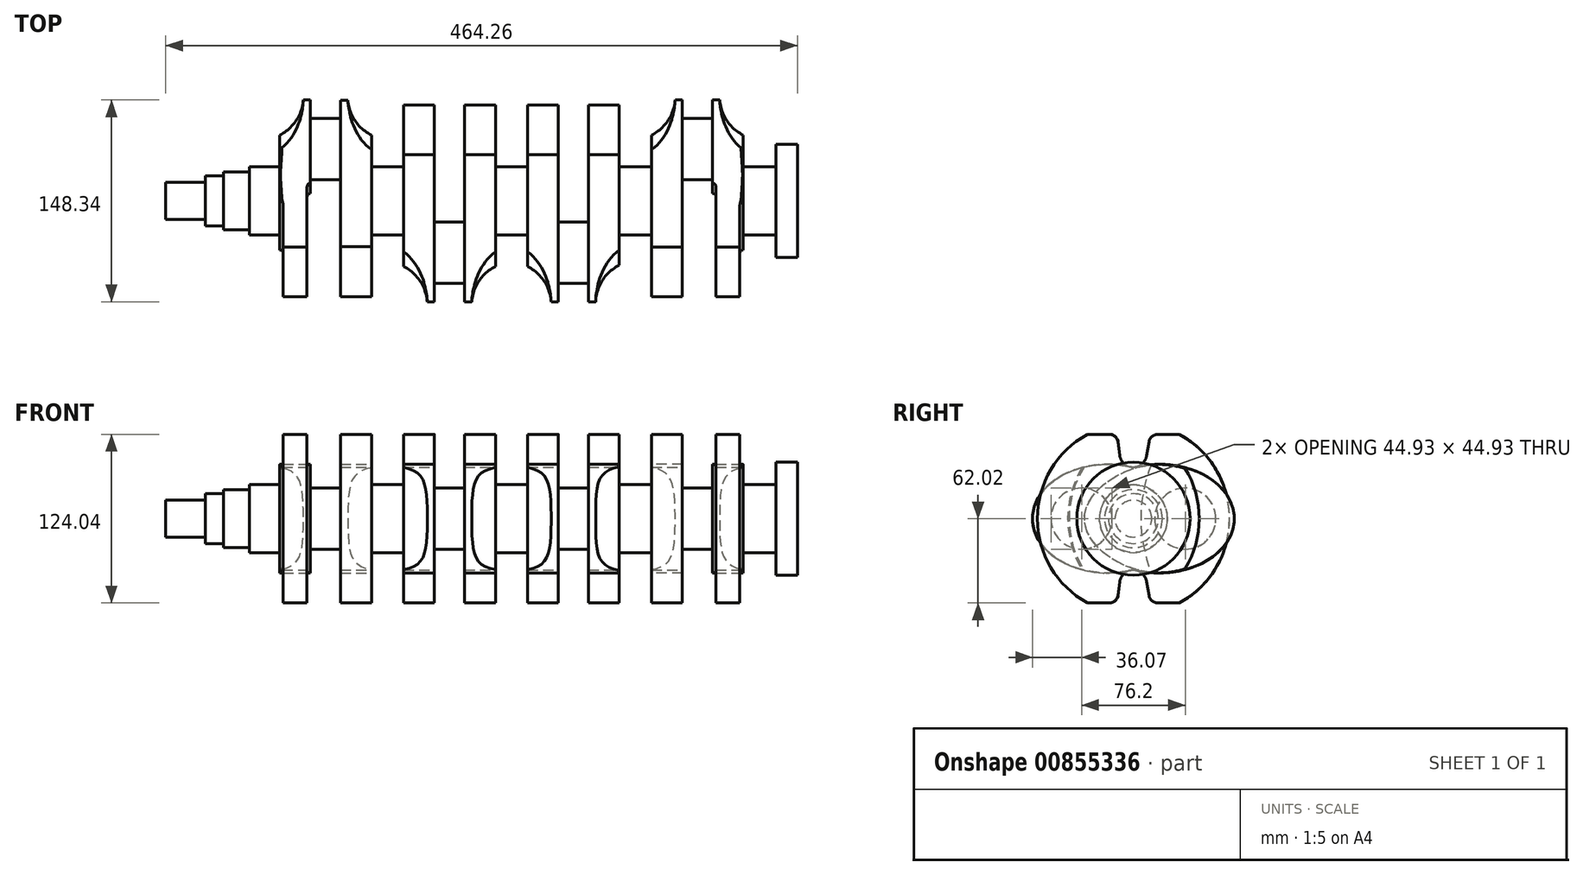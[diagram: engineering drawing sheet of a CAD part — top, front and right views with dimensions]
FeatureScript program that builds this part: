
annotation { "Feature Type Name" : "Feature", "Feature Type Description" : "" }
export const myFeature = defineFeature(function(context is Context, id is Id, definition is map)
    precondition{}
    {
        {
            var Q0;
            Q0=qCreatedBy(makeId("Right.planeOp"),FACE);
            var sketch = newSketch(context, id + "F0", { "sketchPlane" : qUnion([Q0])});
            skLineSegment(sketch, "E0", {"start": v(0, 0) * mm, "end": v(38.1, 0) * mm});
            skLineSegment(sketch, "E1.MirrorCS", {"start": v(0, 0) * mm, "end": v(-38.1, 0) * mm});
            skSolve(sketch);
        }
        {
            var Q0;
            Q0=qCreatedBy(makeId("Front.planeOp"),FACE);
            var sketch = newSketch(context, id + "F1", { "sketchPlane" : qUnion([Q0])});
            skLineSegment(sketch, "E2", {"start": v(-192.37, 24.97) * mm, "end": v(-176.5, 24.97) * mm});
            skLineSegment(sketch, "E3", {"start": v(194.75, 24.97) * mm, "end": v(194.75, 41.6) * mm});
            skLineSegment(sketch, "E4", {"start": v(194.75, 41.6) * mm, "end": v(210.48, 41.6) * mm});
            skLineSegment(sketch, "E5", {"start": v(210.48, 41.6) * mm, "end": v(210.48, 0) * mm});
            skLineSegment(sketch, "E6", {"start": v(-192.37, 24.97) * mm, "end": v(-192.37, 21.27) * mm});
            skLineSegment(sketch, "E7", {"start": v(-192.37, 21.27) * mm, "end": v(-211.42, 21.27) * mm});
            skLineSegment(sketch, "E8", {"start": v(-211.42, 21.27) * mm, "end": v(-211.42, 18.3) * mm});
            skLineSegment(sketch, "E9", {"start": v(-211.42, 18.3) * mm, "end": v(-224.88, 18.3) * mm});
            skLineSegment(sketch, "E10", {"start": v(-224.88, 18.3) * mm, "end": v(-224.88, 13.53) * mm});
            skLineSegment(sketch, "E11", {"start": v(-224.88, 13.53) * mm, "end": v(-253.78, 13.53) * mm});
            skLineSegment(sketch, "E12", {"start": v(-253.78, 0) * mm, "end": v(-253.78, 13.53) * mm});
            skLineSegment(sketch, "E13", {"start": v(-253.78, 0) * mm, "end": v(-176.5, 0) * mm});
            skLineSegment(sketch, "E14.MirrorCS", {"start": v(-192.37, -24.97) * mm, "end": v(194.75, -24.97) * mm, "construction": true});
            skLineSegment(sketch, "E15.MirrorCS", {"start": v(-192.37, -21.27) * mm, "end": v(-211.42, -21.27) * mm, "construction": true});
            skLineSegment(sketch, "E16.MirrorCS", {"start": v(-211.42, -18.3) * mm, "end": v(-224.88, -18.3) * mm, "construction": true});
            skLineSegment(sketch, "E17.MirrorCS", {"start": v(-224.88, -13.53) * mm, "end": v(-253.78, -13.53) * mm, "construction": true});
            skLineSegment(sketch, "E18.MirrorCS", {"start": v(194.75, -41.6) * mm, "end": v(210.48, -41.6) * mm, "construction": true});
            skLineSegment(sketch, "E19", {"start": v(194.75, 24.97) * mm, "end": v(194.75, 0) * mm});
            skLineSegment(sketch, "E20.trimOffspring", {"start": v(194.75, 0) * mm, "end": v(210.48, 0) * mm});
            skLineSegment(sketch, "E21.bottom", {"start": v(-192.37, 24.97) * mm, "end": v(-170.08, 24.97) * mm});
            skLineSegment(sketch, "E21.top", {"start": v(-192.37, 0) * mm, "end": v(-170.08, 0) * mm});
            skLineSegment(sketch, "E21.right", {"start": v(-170.08, 24.97) * mm, "end": v(-170.08, 0) * mm});
            skLineSegment(sketch, "E22", {"start": v(-170.08, 0) * mm, "end": v(194.75, 0) * mm, "construction": true});
            skLineSegment(sketch, "E23", {"start": v(-170.08, 24.97) * mm, "end": v(194.75, 24.97) * mm, "construction": true});
            skLineSegment(sketch, "E24", {"start": v(-170.08, 0) * mm, "end": v(-170.08, -145.17) * mm, "construction": true});
            skLineSegment(sketch, "E25", {"start": v(-170.08, -145.17) * mm, "end": v(-135.68, -145.17) * mm, "construction": true});
            skLineSegment(sketch, "E26", {"start": v(-135.68, -145.17) * mm, "end": v(-135.68, 174.11) * mm, "construction": true});
            skLineSegment(sketch, "E27", {"start": v(-135.68, 174.11) * mm, "end": v(-170.08, 174.11) * mm, "construction": true});
            skLineSegment(sketch, "E28", {"start": v(-170.08, 174.11) * mm, "end": v(-170.08, 24.97) * mm, "construction": true});
            skSolve(sketch);
        }
        {
            var Q0;
            Q0 = qSketchRegion(id + "F1", true);
            var Q1;
            Q1=sQuery(id+"F1.wireOp",EDGE,"E13");
            revolve(context, id + "F2", {"surfaceOperationType" : NewSurfaceOperationType.NEW, "entities" : qUnion([Q0]), "axis" : qUnion([Q1]), "revolveType" : RevolveType.FULL});
        }
        {
            var Q0;
            Q0=makeQuery(id+"F2.opRevolve","SWEPT_FACE",FACE,{"disambiguationData":[OSD([sQuery(id+"F1.wireOp",EDGE,"E6")])]});
            cPlane(context, id + "F3", {"entities" : qUnion([Q0]), "cplaneType" : CPlaneType.OFFSET, "offset" : 33.62 * mm, "oppositeDirection" : true, "width" : 150 * mm, "height" : 150 * mm});
        }
        {
            var Q0;
            Q0=qCreatedBy(id+"F3.planeOp",FACE);
            var sketch = newSketch(context, id + "F4", { "sketchPlane" : qUnion([Q0])});
            skLineSegment(sketch, "E29", {"start": v(-74.17, 0) * mm, "end": v(74.61, 0) * mm, "construction": true});
            skArc(sketch, "E30", {"start": v(33.95, -61.91) * mm, "mid": v(70.61, 0) * mm, "end": v(33.95, 61.91) * mm});
            skLineSegment(sketch, "E31", {"start": v(33.95, 61.91) * mm, "end": v(17.7, 61.91) * mm});
            skLineSegment(sketch, "E32", {"start": v(33.95, -61.91) * mm, "end": v(17.7, -61.91) * mm});
            skArc(sketch, "E33", {"start": v(17.7, 61.91) * mm, "mid": v(13.5, 60.33) * mm, "end": v(11.4, 56.38) * mm});
            skPoint(sketch, "E34.orphan", {"position": v(-76.24, 0) * mm});
            skEllipticalArc(sketch, "E35", {});
            skPoint(sketch, "E36.orphan", {"position": v(-19.05, 39.95) * mm});
            skPoint(sketch, "E37.end.orphan", {"position": v(-17.72, -39.94) * mm});
            skLineSegment(sketch, "E38", {"start": v(10.13, 46.63) * mm, "end": v(11.4, 56.38) * mm});
            skArc(sketch, "E39", {"start": v(-2.24, 38.04) * mm, "mid": v(5.85, 39.6) * mm, "end": v(10.13, 46.63) * mm});
            skArc(sketch, "E40.MirrorCS", {"start": v(17.7, -61.91) * mm, "mid": v(13.5, -60.33) * mm, "end": v(11.4, -56.38) * mm});
            skLineSegment(sketch, "E41.MirrorCS", {"start": v(10.13, -46.63) * mm, "end": v(11.4, -56.38) * mm});
            skArc(sketch, "E42.MirrorCS", {"start": v(-2.24, -38.04) * mm, "mid": v(5.85, -39.6) * mm, "end": v(10.13, -46.63) * mm});
            const initialGuessF4  = {"E35": [-0.01905, 0, -1, 0, 0.055118, 0.03994730190328979, 4.402440832772506, 1.88074447440708]};
            skSetInitialGuess(sketch, initialGuessF4);
            skSolve(sketch);
        }
        {
            var Q0;
            Q0=qCreatedBy(id+"F3.planeOp",FACE);
            cPlane(context, id + "F5", {"entities" : qUnion([Q0]), "cplaneType" : CPlaneType.OFFSET, "offset" : 44.8 * mm, "oppositeDirection" : true, "width" : 150 * mm, "height" : 150 * mm});
        }
        {
            var Q0;
            Q0=qCreatedBy(id+"F5.planeOp",FACE);
            var sketch = newSketch(context, id + "F6", { "sketchPlane" : qUnion([Q0])});
            skEllipticalArc(sketch, "E43", {});
            skArc(sketch, "E44", {"start": v(33.75, -62.02) * mm, "mid": v(70.61, 0) * mm, "end": v(33.75, 62.02) * mm});
            skArc(sketch, "E45", {"start": v(-2.04, 38.05) * mm, "mid": v(6.22, 39.73) * mm, "end": v(10.37, 47.06) * mm});
            skLineSegment(sketch, "E46", {"start": v(17.5, 62.02) * mm, "end": v(33.75, 62.02) * mm});
            skArc(sketch, "E47", {"start": v(17.5, 62.02) * mm, "mid": v(13.2, 60.35) * mm, "end": v(11.17, 56.22) * mm});
            skLineSegment(sketch, "E48", {"start": v(10.37, 47.06) * mm, "end": v(11.17, 56.22) * mm});
            skLineSegment(sketch, "E49.MirrorCS", {"start": v(17.5, -62.02) * mm, "end": v(33.75, -62.02) * mm});
            skArc(sketch, "E50.MirrorCS", {"start": v(17.5, -62.02) * mm, "mid": v(13.2, -60.35) * mm, "end": v(11.17, -56.22) * mm});
            skLineSegment(sketch, "E51.MirrorCS", {"start": v(10.37, -47.06) * mm, "end": v(11.17, -56.22) * mm});
            skArc(sketch, "E52.MirrorCS", {"start": v(-2.04, -38.05) * mm, "mid": v(6.22, -39.73) * mm, "end": v(10.37, -47.06) * mm});
            const initialGuessF6  = {"E43": [-0.018827772470886794, 0, -1, 0, 0.055118, 0.03994730190328979, 4.402958475438665, 1.8807444744070803]};
            skSetInitialGuess(sketch, initialGuessF6);
            skSolve(sketch);
        }
        {
            var Q0;
            Q0=qCreatedBy(id+"F5.planeOp",FACE);
            cPlane(context, id + "F7", {"entities" : qUnion([Q0]), "cplaneType" : CPlaneType.OFFSET, "offset" : 46.31 * mm, "oppositeDirection" : true, "width" : 150 * mm, "height" : 150 * mm});
        }
        {
            var Q0;
            Q0=qCreatedBy(id+"F7.planeOp",FACE);
            var sketch = newSketch(context, id + "F8", { "sketchPlane" : qUnion([Q0])});
            skLineSegment(sketch, "E53", {"start": v(-128.9, 0) * mm, "end": v(74.17, 0) * mm, "construction": true});
            skArc(sketch, "E54", {"start": v(-33.95, 61.91) * mm, "mid": v(-70.61, 0) * mm, "end": v(-33.95, -61.91) * mm});
            skLineSegment(sketch, "E55", {"start": v(74.17, 61.8) * mm, "end": v(74.17, -79.85) * mm, "construction": true});
            skLineSegment(sketch, "E56.trimOffspring", {"start": v(19.08, 39.94) * mm, "end": v(19.08, -39.94) * mm, "construction": true});
            skEllipticalArc(sketch, "E57", {});
            skLineSegment(sketch, "E58", {"start": v(-33.95, 61.91) * mm, "end": v(-17.7, 61.91) * mm});
            skArc(sketch, "E59", {"start": v(-11.4, 56.42) * mm, "mid": v(-13.52, 60.35) * mm, "end": v(-17.7, 61.91) * mm});
            skArc(sketch, "E60", {"start": v(-10.07, 46.57) * mm, "mid": v(-5.77, 39.58) * mm, "end": v(2.3, 38.04) * mm});
            skLineSegment(sketch, "E61", {"start": v(-10.07, 46.57) * mm, "end": v(-11.4, 56.42) * mm});
            skLineSegment(sketch, "E62.MirrorCS", {"start": v(-33.95, -61.91) * mm, "end": v(-17.7, -61.91) * mm});
            skLineSegment(sketch, "E63.MirrorCS", {"start": v(-10.07, -46.57) * mm, "end": v(-11.4, -56.42) * mm});
            skArc(sketch, "E64.MirrorCS", {"start": v(-10.07, -46.57) * mm, "mid": v(-5.77, -39.58) * mm, "end": v(2.3, -38.04) * mm});
            skArc(sketch, "E65.MirrorCS", {"start": v(-11.4, -56.42) * mm, "mid": v(-13.52, -60.35) * mm, "end": v(-17.7, -61.91) * mm});
            const initialGuessF8  = {"E57": [0.019076767620736908, 0, 1, 0, 0.05509123237926309, 0.03994149999999999, 4.4028504044055, 1.8803349027740879]};
            skSetInitialGuess(sketch, initialGuessF8);
            skSolve(sketch);
        }
        {
            var Q0;
            Q0=qCreatedBy(id+"F7.planeOp",FACE);
            cPlane(context, id + "F9", {"entities" : qUnion([Q0]), "cplaneType" : CPlaneType.OFFSET, "offset" : 44.8 * mm, "oppositeDirection" : true, "width" : 150 * mm, "height" : 150 * mm});
        }
        {
            var Q0;
            Q0=qCreatedBy(id+"F9.planeOp",FACE);
            var sketch = newSketch(context, id + "F10", { "sketchPlane" : qUnion([Q0])});
            skArc(sketch, "E66", {"start": v(-33.95, 61.91) * mm, "mid": v(-70.61, 0) * mm, "end": v(-33.95, -61.91) * mm});
            skLineSegment(sketch, "E67", {"start": v(-140.28, 0) * mm, "end": v(97.25, 0) * mm, "construction": true});
            skLineSegment(sketch, "E68", {"start": v(19.05, 39.94) * mm, "end": v(19.05, 0) * mm, "construction": true});
            skPoint(sketch, "E69.trimOffspring.end.orphan", {"position": v(55.02, 61.91) * mm});
            skPoint(sketch, "E70.start.orphan", {"position": v(-109.8, 61.91) * mm});
            skPoint(sketch, "E71.orphan", {"position": v(-109.8, -61.91) * mm});
            skPoint(sketch, "E72.MirrorCS.end.orphan", {"position": v(55.02, -61.91) * mm});
            skEllipticalArc(sketch, "E73", {});
            skLineSegment(sketch, "E74", {"start": v(-33.95, 61.91) * mm, "end": v(-17.7, 61.91) * mm});
            skArc(sketch, "E75", {"start": v(-17.7, 61.91) * mm, "mid": v(-13.6, 60.4) * mm, "end": v(-11.43, 56.6) * mm});
            skLineSegment(sketch, "E76", {"start": v(-11.43, 56.6) * mm, "end": v(-9.73, 46.35) * mm});
            skArc(sketch, "E77", {"start": v(-9.73, 46.35) * mm, "mid": v(-5.37, 39.58) * mm, "end": v(2.55, 38.1) * mm});
            skArc(sketch, "E78.MirrorCS", {"start": v(-9.73, -46.35) * mm, "mid": v(-5.37, -39.58) * mm, "end": v(2.55, -38.1) * mm});
            skLineSegment(sketch, "E79.MirrorCS", {"start": v(-11.43, -56.6) * mm, "end": v(-9.73, -46.35) * mm});
            skArc(sketch, "E80.MirrorCS", {"start": v(-17.7, -61.91) * mm, "mid": v(-13.6, -60.4) * mm, "end": v(-11.43, -56.6) * mm});
            skLineSegment(sketch, "E81.MirrorCS", {"start": v(-33.95, -61.91) * mm, "end": v(-17.7, -61.91) * mm});
            const initialGuessF10  = {"E73": [0.01905, 0, 1, 0, 0.055118, 0.039941500000000005, 4.408302439790269, 1.8748828673893172]};
            skSetInitialGuess(sketch, initialGuessF10);
            skSolve(sketch);
        }
        {
            var Q0;
            Q0=qCreatedBy(id+"F9.planeOp",FACE);
            cPlane(context, id + "F11", {"entities" : qUnion([Q0]), "cplaneType" : CPlaneType.OFFSET, "offset" : 46.31 * mm, "oppositeDirection" : true, "width" : 150 * mm, "height" : 150 * mm});
        }
        {
            var Q0;
            Q0=qCreatedBy(id+"F11.planeOp",FACE);
            var sketch = newSketch(context, id + "F12", { "sketchPlane" : qUnion([Q0])});
            skArc(sketch, "E82", {"start": v(-33.95, 61.91) * mm, "mid": v(-70.61, 0) * mm, "end": v(-33.95, -61.91) * mm});
            skLineSegment(sketch, "E83", {"start": v(-140.28, 0) * mm, "end": v(97.25, 0) * mm, "construction": true});
            skLineSegment(sketch, "E84", {"start": v(19.05, 39.94) * mm, "end": v(19.05, 0) * mm, "construction": true});
            skPoint(sketch, "E85.trimOffspring.end.orphan", {"position": v(69.73, 63.16) * mm});
            skPoint(sketch, "E86.start.orphan", {"position": v(-95.09, 63.16) * mm});
            skPoint(sketch, "E87.orphan", {"position": v(-95.09, -63.16) * mm});
            skPoint(sketch, "E88.MirrorCS.end.orphan", {"position": v(69.73, -63.16) * mm});
            skEllipticalArc(sketch, "E89", {});
            skLineSegment(sketch, "E90", {"start": v(-33.95, 61.91) * mm, "end": v(-17.7, 61.91) * mm});
            skArc(sketch, "E91", {"start": v(-17.7, 61.91) * mm, "mid": v(-13.6, 60.4) * mm, "end": v(-11.43, 56.6) * mm});
            skLineSegment(sketch, "E92", {"start": v(-11.43, 56.6) * mm, "end": v(-9.73, 46.35) * mm});
            skArc(sketch, "E93", {"start": v(-9.73, 46.35) * mm, "mid": v(-5.37, 39.58) * mm, "end": v(2.55, 38.1) * mm});
            skArc(sketch, "E94.MirrorCS", {"start": v(-9.73, -46.35) * mm, "mid": v(-5.37, -39.58) * mm, "end": v(2.55, -38.1) * mm});
            skLineSegment(sketch, "E95.MirrorCS", {"start": v(-11.43, -56.6) * mm, "end": v(-9.73, -46.35) * mm});
            skArc(sketch, "E96.MirrorCS", {"start": v(-17.7, -61.91) * mm, "mid": v(-13.6, -60.4) * mm, "end": v(-11.43, -56.6) * mm});
            skLineSegment(sketch, "E97.MirrorCS", {"start": v(-33.95, -61.91) * mm, "end": v(-17.7, -61.91) * mm});
            const initialGuessF12  = {"E89": [0.01905, 0, 1, 0, 0.055118, 0.039941500000000005, 4.408302439790269, 1.8748828673893168]};
            skSetInitialGuess(sketch, initialGuessF12);
            skSolve(sketch);
        }
        {
            var Q0;
            Q0=qCreatedBy(id+"F11.planeOp",FACE);
            cPlane(context, id + "F13", {"entities" : qUnion([Q0]), "cplaneType" : CPlaneType.OFFSET, "offset" : 44.8 * mm, "oppositeDirection" : true, "width" : 150 * mm, "height" : 150 * mm});
        }
        {
            var Q0;
            Q0=qCreatedBy(id+"F13.planeOp",FACE);
            var sketch = newSketch(context, id + "F14", { "sketchPlane" : qUnion([Q0])});
            skArc(sketch, "E98", {"start": v(-33.95, 61.91) * mm, "mid": v(-70.61, 0) * mm, "end": v(-33.95, -61.91) * mm});
            skLineSegment(sketch, "E99", {"start": v(-140.28, 0) * mm, "end": v(97.25, 0) * mm, "construction": true});
            skLineSegment(sketch, "E100", {"start": v(19.05, 39.94) * mm, "end": v(19.05, 0) * mm, "construction": true});
            skPoint(sketch, "E101.trimOffspring.end.orphan", {"position": v(69.73, 63.16) * mm});
            skPoint(sketch, "E102.start.orphan", {"position": v(-95.09, 63.16) * mm});
            skPoint(sketch, "E103.orphan", {"position": v(-95.09, -63.16) * mm});
            skPoint(sketch, "E104.MirrorCS.end.orphan", {"position": v(69.73, -63.16) * mm});
            skEllipticalArc(sketch, "E105", {});
            skLineSegment(sketch, "E106", {"start": v(-33.95, 61.91) * mm, "end": v(-17.7, 61.91) * mm});
            skArc(sketch, "E107", {"start": v(-17.7, 61.91) * mm, "mid": v(-13.6, 60.4) * mm, "end": v(-11.43, 56.6) * mm});
            skLineSegment(sketch, "E108", {"start": v(-11.43, 56.6) * mm, "end": v(-9.73, 46.35) * mm});
            skArc(sketch, "E109", {"start": v(-9.73, 46.35) * mm, "mid": v(-5.37, 39.58) * mm, "end": v(2.55, 38.1) * mm});
            skArc(sketch, "E110.MirrorCS", {"start": v(-9.73, -46.35) * mm, "mid": v(-5.37, -39.58) * mm, "end": v(2.55, -38.1) * mm});
            skLineSegment(sketch, "E111.MirrorCS", {"start": v(-11.43, -56.6) * mm, "end": v(-9.73, -46.35) * mm});
            skArc(sketch, "E112.MirrorCS", {"start": v(-17.7, -61.91) * mm, "mid": v(-13.6, -60.4) * mm, "end": v(-11.43, -56.6) * mm});
            skLineSegment(sketch, "E113.MirrorCS", {"start": v(-33.95, -61.91) * mm, "end": v(-17.7, -61.91) * mm});
            const initialGuessF14  = {"E105": [0.01905, 0, 1, 0, 0.055118, 0.039941500000000005, 4.408302439790269, 1.8748828673893168]};
            skSetInitialGuess(sketch, initialGuessF14);
            skSolve(sketch);
        }
        {
            var Q0;
            Q0=qCreatedBy(id+"F13.planeOp",FACE);
            cPlane(context, id + "F15", {"entities" : qUnion([Q0]), "cplaneType" : CPlaneType.OFFSET, "offset" : 46.31 * mm, "oppositeDirection" : true, "width" : 150 * mm, "height" : 150 * mm});
        }
        {
            var Q0;
            Q0=qCreatedBy(id+"F15.planeOp",FACE);
            var sketch = newSketch(context, id + "F16", { "sketchPlane" : qUnion([Q0])});
            skLineSegment(sketch, "E114", {"start": v(-74.17, 0) * mm, "end": v(74.61, 0) * mm, "construction": true});
            skArc(sketch, "E115", {"start": v(33.95, -61.91) * mm, "mid": v(70.61, 0) * mm, "end": v(33.95, 61.91) * mm});
            skLineSegment(sketch, "E116", {"start": v(33.95, 61.91) * mm, "end": v(17.7, 61.91) * mm});
            skLineSegment(sketch, "E117", {"start": v(33.95, -61.91) * mm, "end": v(17.7, -61.91) * mm});
            skArc(sketch, "E118", {"start": v(17.7, 61.91) * mm, "mid": v(13.5, 60.33) * mm, "end": v(11.4, 56.38) * mm});
            skPoint(sketch, "E119.orphan", {"position": v(-76.24, 0) * mm});
            skEllipticalArc(sketch, "E120", {});
            skPoint(sketch, "E121.orphan", {"position": v(-19.05, 39.95) * mm});
            skPoint(sketch, "E122.end.orphan", {"position": v(-17.72, -39.94) * mm});
            skLineSegment(sketch, "E123", {"start": v(10.13, 46.63) * mm, "end": v(11.4, 56.38) * mm});
            skArc(sketch, "E124", {"start": v(-2.24, 38.04) * mm, "mid": v(5.85, 39.6) * mm, "end": v(10.13, 46.63) * mm});
            skArc(sketch, "E125.MirrorCS", {"start": v(17.7, -61.91) * mm, "mid": v(13.5, -60.33) * mm, "end": v(11.4, -56.38) * mm});
            skLineSegment(sketch, "E126.MirrorCS", {"start": v(10.13, -46.63) * mm, "end": v(11.4, -56.38) * mm});
            skArc(sketch, "E127.MirrorCS", {"start": v(-2.24, -38.04) * mm, "mid": v(5.85, -39.6) * mm, "end": v(10.13, -46.63) * mm});
            const initialGuessF16  = {"E120": [-0.01905, -8.282725768954612e-07, -1, 0, 0.055118, 0.03994730190328979, 4.402440832772506, 1.8807444744070803]};
            skSetInitialGuess(sketch, initialGuessF16);
            skSolve(sketch);
        }
        {
            var Q0;
            Q0=qCreatedBy(id+"F15.planeOp",FACE);
            cPlane(context, id + "F17", {"entities" : qUnion([Q0]), "cplaneType" : CPlaneType.OFFSET, "offset" : 44.8 * mm, "oppositeDirection" : true, "width" : 150 * mm, "height" : 150 * mm});
        }
        {
            var Q0;
            Q0=qCreatedBy(id+"F17.planeOp",FACE);
            var sketch = newSketch(context, id + "F18", { "sketchPlane" : qUnion([Q0])});
            skLineSegment(sketch, "E128", {"start": v(-74.17, 0) * mm, "end": v(74.61, 0) * mm, "construction": true});
            skArc(sketch, "E129", {"start": v(33.95, -61.91) * mm, "mid": v(70.61, 0) * mm, "end": v(33.95, 61.91) * mm});
            skLineSegment(sketch, "E130", {"start": v(33.95, 61.91) * mm, "end": v(17.7, 61.91) * mm});
            skLineSegment(sketch, "E131", {"start": v(33.95, -61.91) * mm, "end": v(17.7, -61.91) * mm});
            skArc(sketch, "E132", {"start": v(17.7, 61.91) * mm, "mid": v(13.5, 60.33) * mm, "end": v(11.4, 56.38) * mm});
            skPoint(sketch, "E133.orphan", {"position": v(-76.24, 0) * mm});
            skEllipticalArc(sketch, "E134", {});
            skPoint(sketch, "E135.orphan", {"position": v(-19.05, 39.95) * mm});
            skPoint(sketch, "E136.end.orphan", {"position": v(-17.72, -39.94) * mm});
            skLineSegment(sketch, "E137", {"start": v(10.13, 46.63) * mm, "end": v(11.4, 56.38) * mm});
            skArc(sketch, "E138", {"start": v(-2.24, 38.04) * mm, "mid": v(5.85, 39.6) * mm, "end": v(10.13, 46.63) * mm});
            skArc(sketch, "E139.MirrorCS", {"start": v(17.7, -61.91) * mm, "mid": v(13.5, -60.33) * mm, "end": v(11.4, -56.38) * mm});
            skLineSegment(sketch, "E140.MirrorCS", {"start": v(10.13, -46.63) * mm, "end": v(11.4, -56.38) * mm});
            skArc(sketch, "E141.MirrorCS", {"start": v(-2.24, -38.04) * mm, "mid": v(5.85, -39.6) * mm, "end": v(10.13, -46.63) * mm});
            const initialGuessF18  = {"E134": [-0.01905, 0, -1, 0, 0.055118, 0.03994730190328979, 4.402440832772506, 1.88074447440708]};
            skSetInitialGuess(sketch, initialGuessF18);
            skSolve(sketch);
        }
        {
            var Q0;
            Q0 = qSketchRegion(id + "F4", true);
            var Q1;
            Q1 = qConstructionFilter(qBodyType(qCreatedBy(id + "F4" ,EDGE), BodyType.WIRE), ConstructionObject.NO);
            extrude(context, id + "F19", {"entities" : qUnion([Q0]), "operationType" : NewBodyOperationType.ADD, "surfaceOperationType" : NewSurfaceOperationType.ADD, "surfaceEntities" : qUnion([Q1]), "endBound" : BoundingType.SYMMETRIC, "depth" : 22.66 * mm, "offsetDistance" : 25 * mm});
        }
        {
            var Q0;
            Q0 = qSketchRegion(id + "F6", true);
            extrude(context, id + "F20", {"entities" : qUnion([Q0]), "operationType" : NewBodyOperationType.ADD, "endBound" : BoundingType.SYMMETRIC, "depth" : 22.66 * mm, "offsetDistance" : 25 * mm});
        }
        {
            var Q0;
            Q0 = qSketchRegion(id + "F8", true);
            extrude(context, id + "F21", {"entities" : qUnion([Q0]), "operationType" : NewBodyOperationType.ADD, "endBound" : BoundingType.SYMMETRIC, "depth" : 22.66 * mm, "offsetDistance" : 25 * mm});
        }
        {
            var Q0;
            Q0 = qSketchRegion(id + "F10", true);
            extrude(context, id + "F22", {"entities" : qUnion([Q0]), "operationType" : NewBodyOperationType.ADD, "endBound" : BoundingType.SYMMETRIC, "depth" : 22.66 * mm, "offsetDistance" : 25 * mm});
        }
        {
            var Q0;
            Q0 = qSketchRegion(id + "F12", true);
            extrude(context, id + "F23", {"entities" : qUnion([Q0]), "operationType" : NewBodyOperationType.ADD, "endBound" : BoundingType.SYMMETRIC, "depth" : 22.66 * mm, "offsetDistance" : 25 * mm});
        }
        {
            var Q0;
            Q0 = qSketchRegion(id + "F14", true);
            extrude(context, id + "F24", {"entities" : qUnion([Q0]), "operationType" : NewBodyOperationType.ADD, "endBound" : BoundingType.SYMMETRIC, "depth" : 22.66 * mm, "offsetDistance" : 25 * mm});
        }
        {
            var Q0;
            Q0 = qSketchRegion(id + "F16", true);
            extrude(context, id + "F25", {"entities" : qUnion([Q0]), "operationType" : NewBodyOperationType.ADD, "endBound" : BoundingType.SYMMETRIC, "depth" : 22.66 * mm, "offsetDistance" : 25 * mm});
        }
        {
            var Q0;
            Q0 = qSketchRegion(id + "F18", true);
            extrude(context, id + "F26", {"entities" : qUnion([Q0]), "operationType" : NewBodyOperationType.ADD, "endBound" : BoundingType.SYMMETRIC, "depth" : 22.66 * mm, "offsetDistance" : 25 * mm});
        }
        {
            var Q0;
            Q0=qCreatedBy(makeId("Front.planeOp"),FACE);
            var sketch = newSketch(context, id + "F27", { "sketchPlane" : qUnion([Q0])});
            skLineSegment(sketch, "E142.bottom", {"start": v(-147.33, 62.1) * mm, "end": v(-125.3, 62.1) * mm});
            skLineSegment(sketch, "E142.top", {"start": v(-147.33, -62.02) * mm, "end": v(-125.3, -62.02) * mm});
            skLineSegment(sketch, "E142.left", {"start": v(-147.33, 62.1) * mm, "end": v(-147.33, -62.02) * mm});
            skLineSegment(sketch, "E142.right", {"start": v(-125.3, 62.1) * mm, "end": v(-125.3, -62.02) * mm});
            skLineSegment(sketch, "E143.bottom", {"start": v(-56.32, 61.92) * mm, "end": v(-34.18, 61.92) * mm});
            skLineSegment(sketch, "E143.top", {"start": v(-56.32, -61.91) * mm, "end": v(-34.18, -61.91) * mm});
            skLineSegment(sketch, "E143.left", {"start": v(-56.32, 61.92) * mm, "end": v(-56.32, -61.91) * mm});
            skLineSegment(sketch, "E143.right", {"start": v(-34.18, 61.92) * mm, "end": v(-34.18, -61.91) * mm});
            skLineSegment(sketch, "E144.bottom", {"start": v(34.8, 61.92) * mm, "end": v(56.92, 61.92) * mm});
            skLineSegment(sketch, "E144.top", {"start": v(34.8, -61.91) * mm, "end": v(56.92, -61.91) * mm});
            skLineSegment(sketch, "E144.left", {"start": v(34.8, 61.92) * mm, "end": v(34.8, -61.91) * mm});
            skLineSegment(sketch, "E144.right", {"start": v(56.92, 61.92) * mm, "end": v(56.92, -61.91) * mm});
            skLineSegment(sketch, "E145.bottom", {"start": v(125.9, 61.92) * mm, "end": v(148.02, 61.92) * mm});
            skLineSegment(sketch, "E145.top", {"start": v(125.9, -61.91) * mm, "end": v(148.02, -61.91) * mm});
            skLineSegment(sketch, "E145.left", {"start": v(125.9, 61.92) * mm, "end": v(125.9, -61.91) * mm});
            skLineSegment(sketch, "E145.right", {"start": v(148.02, 61.92) * mm, "end": v(148.02, -61.91) * mm});
            skSolve(sketch);
        }
        {
            var Q0;
            Q0 = qSketchRegion(id + "F27", true);
            extrude(context, id + "F28", {"entities" : qUnion([Q0]), "operationType" : NewBodyOperationType.REMOVE, "endBound" : BoundingType.THROUGH_ALL, "depth" : 25 * mm, "offsetDistance" : 25 * mm});
        }
        {
            var Q0;
            Q0 = qSketchRegion(id + "F27", true);
            extrude(context, id + "F29", {"entities" : qUnion([Q0]), "operationType" : NewBodyOperationType.REMOVE, "endBound" : BoundingType.THROUGH_ALL, "oppositeDirection" : true, "depth" : 25 * mm, "offsetDistance" : 25 * mm});
        }
        {
            var Q0;
            Q0=qCreatedBy(makeId("Front.planeOp"),FACE);
            var sketch = newSketch(context, id + "F30", { "sketchPlane" : qUnion([Q0])});
            skLineSegment(sketch, "E146", {"start": v(-196.31, 0) * mm, "end": v(-75.66, 0) * mm, "construction": true});
            skLineSegment(sketch, "E147", {"start": v(-199.63, 24.97) * mm, "end": v(179.85, 24.97) * mm, "construction": true});
            skLineSegment(sketch, "E148.MirrorCS", {"start": v(-199.63, -24.97) * mm, "end": v(-107.32, -24.97) * mm, "construction": true});
            skLineSegment(sketch, "E149.bottom", {"start": v(-107.32, 24.97) * mm, "end": v(-75.66, 24.97) * mm});
            skLineSegment(sketch, "E149.left", {"start": v(-107.32, 24.97) * mm, "end": v(-107.32, 0) * mm});
            skLineSegment(sketch, "E149.right", {"start": v(-75.66, 24.97) * mm, "end": v(-75.66, 0) * mm});
            skPoint(sketch, "E150.firstSnap0", {"position": v(-14.32, 0) * mm});
            skLineSegment(sketch, "E150.bottom", {"start": v(-14.32, 24.97) * mm, "end": v(16.9, 24.97) * mm});
            skLineSegment(sketch, "E150.left", {"start": v(-14.32, 24.97) * mm, "end": v(-14.32, 0) * mm});
            skLineSegment(sketch, "E150.right", {"start": v(16.9, 24.97) * mm, "end": v(16.9, 0) * mm});
            skLineSegment(sketch, "E151.bottom", {"start": v(76.32, 24.97) * mm, "end": v(107.99, 24.97) * mm});
            skLineSegment(sketch, "E151.left", {"start": v(76.32, 24.97) * mm, "end": v(76.32, 0) * mm});
            skLineSegment(sketch, "E151.right", {"start": v(107.99, 24.97) * mm, "end": v(107.99, 0) * mm});
            skLineSegment(sketch, "E152.bottom", {"start": v(167.68, 24.97) * mm, "end": v(200.54, 24.97) * mm});
            skLineSegment(sketch, "E152.right", {"start": v(200.54, 24.97) * mm, "end": v(200.54, 0) * mm});
            skLineSegment(sketch, "E153", {"start": v(-107.32, 0) * mm, "end": v(-75.66, 0) * mm});
            skLineSegment(sketch, "E154.trimOffspring", {"start": v(-14.32, 0) * mm, "end": v(16.9, 0) * mm, "construction": true});
            skLineSegment(sketch, "E155.trimOffspring", {"start": v(-14.32, 0) * mm, "end": v(16.9, 0) * mm});
            skLineSegment(sketch, "E156.trimOffspring", {"start": v(76.32, 0) * mm, "end": v(107.99, 0) * mm, "construction": true});
            skLineSegment(sketch, "E157.trimOffspring", {"start": v(76.32, 0) * mm, "end": v(107.99, 0) * mm});
            skPoint(sketch, "E158.orphan", {"position": v(167.68, 0) * mm});
            skLineSegment(sketch, "E159.trimOffspring", {"start": v(167.68, 0) * mm, "end": v(200.54, 0) * mm});
            skPoint(sketch, "E160.orphan", {"position": v(107.99, -24.97) * mm});
            skLineSegment(sketch, "E161.bottom", {"start": v(167.68, 24.97) * mm, "end": v(161.4, 24.97) * mm});
            skLineSegment(sketch, "E161.top", {"start": v(167.68, 0) * mm, "end": v(161.4, 0) * mm});
            skLineSegment(sketch, "E161.right", {"start": v(161.4, 24.97) * mm, "end": v(161.4, 0) * mm});
            skSolve(sketch);
        }
        {
            var Q0;
            Q0 = qSketchRegion(id + "F30", true);
            var Q1;
            Q1=sQuery(id+"F30.wireOp",EDGE,"E153");
            revolve(context, id + "F31", {"operationType" : NewBodyOperationType.ADD, "surfaceOperationType" : NewSurfaceOperationType.NEW, "entities" : qUnion([Q0]), "axis" : qUnion([Q1]), "revolveType" : RevolveType.FULL});
        }
        {
            var Q0;
            Q0=makeQuery(id+"F19.opExtrude","CAP_FACE",FACE,{"disambiguationData":[OSD([sQuery(id+"F4.wireOp",EDGE,"E30"),sQuery(id+"F4.wireOp",EDGE,"E31"),sQuery(id+"F4.wireOp",EDGE,"E32"),sQuery(id+"F4.wireOp",EDGE,"E33"),sQuery(id+"F4.wireOp",EDGE,"E35"),sQuery(id+"F4.wireOp",EDGE,"E38"),sQuery(id+"F4.wireOp",EDGE,"E39"),sQuery(id+"F4.wireOp",EDGE,"E40.MirrorCS"),sQuery(id+"F4.wireOp",EDGE,"E41.MirrorCS"),sQuery(id+"F4.wireOp",EDGE,"E42.MirrorCS")])],"isStart":true});
            var sketch = newSketch(context, id + "F32", { "sketchPlane" : qUnion([Q0])});
            skCircle(sketch, "E162", {"center": v(38.1, 0) * mm, "radius": 22.47 * mm});
            skSolve(sketch);
        }
        {
            var Q0;
            Q0 = qSketchRegion(id + "F32", true);
            extrude(context, id + "F33", {"entities" : qUnion([Q0]), "operationType" : NewBodyOperationType.ADD, "endBound" : BoundingType.UP_TO_NEXT, "depth" : 25 * mm, "offsetDistance" : 25 * mm});
        }
        {
            var Q0;
            Q0=makeQuery(id+"F25.opExtrude","CAP_FACE",FACE,{"disambiguationData":[OSD([sQuery(id+"F16.wireOp",EDGE,"E115"),sQuery(id+"F16.wireOp",EDGE,"E116"),sQuery(id+"F16.wireOp",EDGE,"E117"),sQuery(id+"F16.wireOp",EDGE,"E118"),sQuery(id+"F16.wireOp",EDGE,"E120"),sQuery(id+"F16.wireOp",EDGE,"E123"),sQuery(id+"F16.wireOp",EDGE,"E124"),sQuery(id+"F16.wireOp",EDGE,"E125.MirrorCS"),sQuery(id+"F16.wireOp",EDGE,"E126.MirrorCS"),sQuery(id+"F16.wireOp",EDGE,"E127.MirrorCS")])],"isStart":true});
            var sketch = newSketch(context, id + "F34", { "sketchPlane" : qUnion([Q0])});
            skCircle(sketch, "E163", {"center": v(38.1, 0) * mm, "radius": 22.47 * mm});
            skSolve(sketch);
        }
        {
            var Q0;
            Q0 = qSketchRegion(id + "F34", true);
            extrude(context, id + "F35", {"entities" : qUnion([Q0]), "operationType" : NewBodyOperationType.ADD, "endBound" : BoundingType.UP_TO_NEXT, "depth" : 25 * mm, "offsetDistance" : 25 * mm});
        }
        {
            var Q0;
            Q0=makeQuery(id+"F21.opExtrude","CAP_FACE",FACE,{"disambiguationData":[OSD([sQuery(id+"F8.wireOp",EDGE,"E54"),sQuery(id+"F8.wireOp",EDGE,"E57"),sQuery(id+"F8.wireOp",EDGE,"E58"),sQuery(id+"F8.wireOp",EDGE,"E59"),sQuery(id+"F8.wireOp",EDGE,"E60"),sQuery(id+"F8.wireOp",EDGE,"E61"),sQuery(id+"F8.wireOp",EDGE,"E62.MirrorCS"),sQuery(id+"F8.wireOp",EDGE,"E63.MirrorCS"),sQuery(id+"F8.wireOp",EDGE,"E64.MirrorCS"),sQuery(id+"F8.wireOp",EDGE,"E65.MirrorCS")])],"isStart":true});
            var sketch = newSketch(context, id + "F36", { "sketchPlane" : qUnion([Q0])});
            skCircle(sketch, "E164", {"center": v(-38.1, 0) * mm, "radius": 22.47 * mm});
            skSolve(sketch);
        }
        {
            var Q0;
            Q0 = qSketchRegion(id + "F36", true);
            extrude(context, id + "F37", {"entities" : qUnion([Q0]), "operationType" : NewBodyOperationType.ADD, "endBound" : BoundingType.UP_TO_NEXT, "depth" : 25 * mm, "offsetDistance" : 25 * mm});
        }
        {
            var Q0;
            Q0=makeQuery(id+"F23.opExtrude","CAP_FACE",FACE,{"disambiguationData":[OSD([sQuery(id+"F12.wireOp",EDGE,"E82"),sQuery(id+"F12.wireOp",EDGE,"E89"),sQuery(id+"F12.wireOp",EDGE,"E90"),sQuery(id+"F12.wireOp",EDGE,"E91"),sQuery(id+"F12.wireOp",EDGE,"E92"),sQuery(id+"F12.wireOp",EDGE,"E93"),sQuery(id+"F12.wireOp",EDGE,"E94.MirrorCS"),sQuery(id+"F12.wireOp",EDGE,"E95.MirrorCS"),sQuery(id+"F12.wireOp",EDGE,"E96.MirrorCS"),sQuery(id+"F12.wireOp",EDGE,"E97.MirrorCS")])],"isStart":true});
            var sketch = newSketch(context, id + "F38", { "sketchPlane" : qUnion([Q0])});
            skCircle(sketch, "E165", {"center": v(-38.1, 0) * mm, "radius": 22.47 * mm});
            skSolve(sketch);
        }
        {
            var Q0;
            Q0 = qSketchRegion(id + "F38", true);
            var Q1;
            Q1=makeQuery(id+"F2.opRevolve","SWEPT_BODY",BODY,{"disambiguationData":[OSD([sQuery(id+"F1.wireOp",EDGE,"E7"),sQuery(id+"F1.wireOp",EDGE,"E8"),sQuery(id+"F1.wireOp",EDGE,"E9"),sQuery(id+"F1.wireOp",EDGE,"E10"),sQuery(id+"F1.wireOp",EDGE,"E11"),sQuery(id+"F1.wireOp",EDGE,"E12"),sQuery(id+"F1.wireOp",EDGE,"E13"),sQuery(id+"F1.wireOp",EDGE,"E21.bottom"),sQuery(id+"F1.wireOp",EDGE,"E21.top"),sQuery(id+"F1.wireOp",EDGE,"E6"),sQuery(id+"F1.wireOp",EDGE,"E21.right")])]});
            extrude(context, id + "F39", {"entities" : qUnion([Q0]), "operationType" : NewBodyOperationType.ADD, "endBound" : BoundingType.UP_TO_NEXT, "depth" : 25 * mm, "endBoundEntityBody" : qUnion([Q1]), "offsetDistance" : 25 * mm});
        }
        {
            var Q0;
            Q0=makeQuery(id+"F19.opExtrude","CAP_FACE",FACE,{"disambiguationData":[OSD([sQuery(id+"F4.wireOp",EDGE,"E30"),sQuery(id+"F4.wireOp",EDGE,"E31"),sQuery(id+"F4.wireOp",EDGE,"E32"),sQuery(id+"F4.wireOp",EDGE,"E33"),sQuery(id+"F4.wireOp",EDGE,"E35"),sQuery(id+"F4.wireOp",EDGE,"E38"),sQuery(id+"F4.wireOp",EDGE,"E39"),sQuery(id+"F4.wireOp",EDGE,"E40.MirrorCS"),sQuery(id+"F4.wireOp",EDGE,"E41.MirrorCS"),sQuery(id+"F4.wireOp",EDGE,"E42.MirrorCS")])],"isStart":false});
            var sketch = newSketch(context, id + "F40", { "sketchPlane" : qUnion([Q0])});
            skArc(sketch, "E166", {"start": v(38.53, 36.76) * mm, "mid": v(-95.07, 0) * mm, "end": v(38.53, -36.76) * mm});
            skLineSegment(sketch, "E167", {"start": v(-95.07, 0) * mm, "end": v(-95.07, -84.54) * mm, "construction": true});
            skLineSegment(sketch, "E168", {"start": v(-24.97, 0) * mm, "end": v(-24.97, -70) * mm, "construction": true});
            skPoint(sketch, "E169", {"position": v(38.53, -36.76) * mm});
            skPoint(sketch, "E170.MirrorP", {"position": v(38.53, 36.76) * mm});
            skArc(sketch, "E171", {"start": v(38.53, -36.76) * mm, "mid": v(48.65, 0) * mm, "end": v(38.53, 36.76) * mm});
            skLineSegment(sketch, "E172", {"start": v(0, 0) * mm, "end": v(0, -107.24) * mm, "construction": true});
            skArc(sketch, "E173.MirrorCS", {"start": v(-38.53, 36.76) * mm, "mid": v(95.07, 0) * mm, "end": v(-38.53, -36.76) * mm});
            skArc(sketch, "E174.MirrorCS", {"start": v(-38.53, -36.76) * mm, "mid": v(-48.65, 0) * mm, "end": v(-38.53, 36.76) * mm});
            skSolve(sketch);
        }
        {
            var Q0;
            Q0=qCreatedBy(makeId("Top.planeOp"),FACE);
            var sketch = newSketch(context, id + "F41", { "sketchPlane" : qUnion([Q0])});
            skLineSegment(sketch, "E175", {"start": v(0, 0) * mm, "end": v(-240.43, 0) * mm, "construction": true});
            skPoint(sketch, "E176", {"position": v(-56.32, 72.65) * mm});
            skLineSegment(sketch, "E177", {"start": v(-61.52, 72.65) * mm, "end": v(-93.27, 72.65) * mm});
            skArc(sketch, "E178", {"start": v(-61.52, 72.65) * mm, "mid": v(-70.82, 50.2) * mm, "end": v(-93.27, 40.9) * mm});
            skLineSegment(sketch, "E179", {"start": v(-93.27, 72.65) * mm, "end": v(-93.27, 40.9) * mm});
            skLineSegment(sketch, "E180", {"start": v(153.23, 76.65) * mm, "end": v(184.98, 76.65) * mm});
            skArc(sketch, "E181", {"start": v(153.23, 76.65) * mm, "mid": v(162.53, 54.2) * mm, "end": v(184.98, 44.9) * mm});
            skLineSegment(sketch, "E182", {"start": v(184.98, 76.65) * mm, "end": v(184.98, 44.9) * mm});
            skLineSegment(sketch, "E183", {"start": v(120.69, 76.65) * mm, "end": v(88.94, 76.65) * mm});
            skArc(sketch, "E184", {"start": v(120.69, 76.65) * mm, "mid": v(111.39, 54.2) * mm, "end": v(88.94, 44.9) * mm});
            skLineSegment(sketch, "E185", {"start": v(88.94, 76.65) * mm, "end": v(88.94, 44.9) * mm});
            skLineSegment(sketch, "E186", {"start": v(-120.08, 76.65) * mm, "end": v(-88.33, 76.65) * mm});
            skArc(sketch, "E187", {"start": v(-120.08, 76.65) * mm, "mid": v(-110.78, 54.2) * mm, "end": v(-88.33, 44.9) * mm});
            skLineSegment(sketch, "E188", {"start": v(-88.33, 44.9) * mm, "end": v(-88.33, 76.65) * mm});
            skLineSegment(sketch, "E189", {"start": v(-152.62, 76.65) * mm, "end": v(-184.37, 76.65) * mm});
            skArc(sketch, "E190", {"start": v(-152.62, 76.65) * mm, "mid": v(-161.92, 54.2) * mm, "end": v(-184.37, 44.9) * mm});
            skLineSegment(sketch, "E191", {"start": v(-184.37, 44.9) * mm, "end": v(-184.37, 76.65) * mm});
            skPoint(sketch, "E192.MirrorP", {"position": v(56.92, -71.6) * mm});
            skLineSegment(sketch, "E193", {"start": v(56.92, -71.6) * mm, "end": v(56.92, -75.6) * mm});
            skLineSegment(sketch, "E194", {"start": v(56.92, -75.6) * mm, "end": v(62.13, -75.6) * mm, "construction": true});
            skLineSegment(sketch, "E195", {"start": v(62.13, -75.6) * mm, "end": v(93.88, -75.6) * mm});
            skArc(sketch, "E196", {"start": v(62.13, -75.6) * mm, "mid": v(71.43, -53.15) * mm, "end": v(93.88, -43.86) * mm});
            skLineSegment(sketch, "E197", {"start": v(93.88, -43.86) * mm, "end": v(93.88, -75.6) * mm});
            skLineSegment(sketch, "E198", {"start": v(29.58, -76.63) * mm, "end": v(-2.24, -76.63) * mm});
            skPoint(sketch, "E199", {"position": v(-2.17, -76.63) * mm});
            skArc(sketch, "E200", {"start": v(29.58, -76.63) * mm, "mid": v(20.28, -54.18) * mm, "end": v(-2.17, -44.88) * mm});
            skLineSegment(sketch, "E201", {"start": v(-2.17, -44.88) * mm, "end": v(-2.17, -76.63) * mm});
            skArc(sketch, "E202", {"start": v(-28.98, -76.63) * mm, "mid": v(-19.68, -54.18) * mm, "end": v(2.77, -44.88) * mm});
            skLineSegment(sketch, "E203", {"start": v(2.77, -76.63) * mm, "end": v(2.77, -44.88) * mm});
            skLineSegment(sketch, "E204", {"start": v(-28.98, -76.63) * mm, "end": v(2.77, -76.63) * mm});
            skLineSegment(sketch, "E205", {"start": v(-61.52, -76.65) * mm, "end": v(-93.27, -76.65) * mm});
            skArc(sketch, "E206", {"start": v(-61.52, -76.65) * mm, "mid": v(-70.82, -54.2) * mm, "end": v(-93.27, -44.9) * mm});
            skLineSegment(sketch, "E207", {"start": v(-93.27, -76.65) * mm, "end": v(-93.27, -44.9) * mm});
            skSolve(sketch);
        }
        {
            var Q0;
            Q0=makeQuery(id+"F41.imprint","IMPRINT",FACE,{"disambiguationData":[TD([[makeQuery(id+"F41.imprint","IMPRINT",EDGE,{"derivedFrom":sQuery(id+"F41.wireOp",EDGE,"E180")}),-1.0]])]});
            var Q1;
            Q1=makeQuery(id+"F41.imprint","IMPRINT",FACE,{"disambiguationData":[TD([[makeQuery(id+"F41.imprint","IMPRINT",EDGE,{"derivedFrom":sQuery(id+"F41.wireOp",EDGE,"E183")}),1.0]])]});
            var Q2;
            {var subQ1=sQuery(id+"F41.wireOp",EDGE,"E186");Q2=makeQuery(id+"F41.imprint","IMPRINT",FACE,{"disambiguationData":[TD([[makeQuery(id+"F41.imprint","IMPRINT",EDGE,{"derivedFrom":subQ1}),-1.0]])]});}
            var Q3;
            Q3=makeQuery(id+"F41.imprint","IMPRINT",FACE,{"disambiguationData":[TD([[makeQuery(id+"F41.imprint","IMPRINT",EDGE,{"derivedFrom":sQuery(id+"F41.wireOp",EDGE,"E189")}),1.0]])]});
            var Q4;
            Q4=sQuery(id+"F40.wireOp",EDGE,"E173.MirrorCS");
            var Q5;
            Q5=sQuery(id+"F40.wireOp",EDGE,"E174.MirrorCS");
            sweep(context, id + "F42", {"operationType" : NewBodyOperationType.REMOVE, "profiles" : qUnion([Q0, Q1, Q2, Q3]), "path" : qUnion([Q4, Q5])});
        }
        {
            var Q0;
            Q0=makeQuery(id+"F41.imprint","IMPRINT",FACE,{"disambiguationData":[TD([[makeQuery(id+"F41.imprint","IMPRINT",EDGE,{"derivedFrom":sQuery(id+"F41.wireOp",EDGE,"E195")}),1.0]])]});
            var Q1;
            {var subQ0=sQuery(id+"F41.wireOp",EDGE,"E198");Q1=makeQuery(id+"F41.imprint","IMPRINT",FACE,{"disambiguationData":[TD([[makeQuery(id+"F41.imprint","IMPRINT",EDGE,{"derivedFrom":subQ0}),-1.0]])]});}
            var Q2;
            {var subQ0=sQuery(id+"F41.wireOp",EDGE,"E204");var subQ6=makeQuery(id+"F41.imprint","IMPRINT",VERTEX,{"derivedFrom":subQ0});Q2=makeQuery(id+"F41.imprint","IMPRINT",FACE,{"disambiguationData":[TD([[makeQuery(id+"F41.imprint","IMPRINT",EDGE,{"disambiguationData":[TD([[subQ6,1.0]])],"derivedFrom":subQ0}),1.0]])]});}
            var Q3;
            Q3=makeQuery(id+"F41.imprint","IMPRINT",FACE,{"disambiguationData":[TD([[makeQuery(id+"F41.imprint","IMPRINT",EDGE,{"derivedFrom":sQuery(id+"F41.wireOp",EDGE,"E205")}),-1.0]])]});
            var Q4;
            Q4=sQuery(id+"F40.wireOp",EDGE,"E166");
            var Q5;
            Q5=sQuery(id+"F40.wireOp",EDGE,"E171");
            sweep(context, id + "F43", {"operationType" : NewBodyOperationType.REMOVE, "profiles" : qUnion([Q0, Q1, Q2, Q3]), "path" : qUnion([Q4, Q5])});
        }
        {
            var Q0;
            Q0=makeQuery(id+"F2.opRevolve","SWEPT_FACE",FACE,{"disambiguationData":[OSD([sQuery(id+"F1.wireOp",EDGE,"E5")])]});
            var sketch = newSketch(context, id + "F44", { "sketchPlane" : qUnion([Q0])});
            skCircle(sketch, "E208", {"center": v(0, 0) * mm, "radius": 33.46 * mm});
            skLineSegment(sketch, "E209", {"start": v(98.64, 0) * mm, "end": v(-99.2, 0) * mm, "construction": true});
            skFitSpline(sketch, "E210", {"points": [v(-36.13, 0) * mm, v(19.05, 39.94) * mm, v(74.23, 0) * mm, v(19.05, -39.94) * mm, v(-36.13, 0) * mm]});
            skCircle(sketch, "E211", {"center": v(-36.13, 0) * mm, "radius": 36.07 * mm});
            skCircle(sketch, "E212", {"center": v(38.1, 0) * mm, "radius": 29.21 * mm});
            skLineSegment(sketch, "E213", {"start": v(19.05, 39.94) * mm, "end": v(19.05, -39.94) * mm, "construction": true});
            skLineSegment(sketch, "E214", {"start": v(74.23, 0) * mm, "end": v(-36.13, 0) * mm, "construction": true});
            skCircle(sketch, "E215", {"center": v(112.15, 0) * mm, "radius": 106.68 * mm});
            skSolve(sketch);
        }
        {
            var Q0;
            Q0=qCreatedBy(makeId("Top.planeOp"),FACE);
            var sketch = newSketch(context, id + "F45", { "sketchPlane" : qUnion([Q0])});
            skLineSegment(sketch, "E216", {"start": v(-147.42, -83.31) * mm, "end": v(-147.42, 5.47) * mm});
            skLineSegment(sketch, "E217", {"start": v(-147.42, -83.31) * mm, "end": v(-149.96, -83.31) * mm});
            skLineSegment(sketch, "E218", {"start": v(-149.96, -83.31) * mm, "end": v(-149.96, 2.93) * mm});
            skArc(sketch, "E219", {"start": v(-147.42, 5.47) * mm, "mid": v(-149.21, 4.73) * mm, "end": v(-149.96, 2.93) * mm});
            skLineSegment(sketch, "E220", {"start": v(-167.54, -83.31) * mm, "end": v(-167.54, -38.6) * mm});
            skLineSegment(sketch, "E221", {"start": v(-167.54, -83.31) * mm, "end": v(-170.08, -83.31) * mm});
            skArc(sketch, "E222", {"start": v(-167.54, -38.6) * mm, "mid": v(-168.29, -36.81) * mm, "end": v(-170.08, -36.07) * mm});
            skLineSegment(sketch, "E223", {"start": v(-170.08, -83.31) * mm, "end": v(-170.08, -36.07) * mm});
            skLineSegment(sketch, "E224", {"start": v(148.02, -83.31) * mm, "end": v(148.02, 5.47) * mm});
            skLineSegment(sketch, "E225", {"start": v(148.02, -83.31) * mm, "end": v(150.56, -83.31) * mm});
            skArc(sketch, "E226", {"start": v(148.02, 5.47) * mm, "mid": v(149.82, 4.73) * mm, "end": v(150.56, 2.93) * mm});
            skLineSegment(sketch, "E227", {"start": v(150.56, -83.31) * mm, "end": v(150.56, 2.93) * mm});
            skLineSegment(sketch, "E228", {"start": v(168.15, -83.31) * mm, "end": v(168.15, -38.6) * mm});
            skLineSegment(sketch, "E229", {"start": v(168.15, -83.31) * mm, "end": v(170.69, -83.31) * mm});
            skLineSegment(sketch, "E230", {"start": v(170.69, -83.31) * mm, "end": v(170.69, -36.07) * mm});
            skArc(sketch, "E231", {"start": v(170.69, -36.07) * mm, "mid": v(168.9, -36.81) * mm, "end": v(168.15, -38.6) * mm});
            skSolve(sketch);
        }
        {
            var Q0;
            Q0=makeQuery(id+"F45.imprint","IMPRINT",FACE,{"disambiguationData":[TD([[makeQuery(id+"F45.imprint","IMPRINT",EDGE,{"derivedFrom":sQuery(id+"F45.wireOp",EDGE,"E228")}),-1.0]])]});
            var Q1;
            Q1=makeQuery(id+"F45.imprint","IMPRINT",FACE,{"disambiguationData":[TD([[makeQuery(id+"F45.imprint","IMPRINT",EDGE,{"derivedFrom":sQuery(id+"F45.wireOp",EDGE,"E220")}),1.0]])]});
            var Q2;
            Q2=sQuery(id+"F44.wireOp",EDGE,"E210");
            sweep(context, id + "F46", {"operationType" : NewBodyOperationType.REMOVE, "profiles" : qUnion([Q0, Q1]), "path" : qUnion([Q2])});
        }
        {
            var Q0;
            Q0=makeQuery(id+"F45.imprint","IMPRINT",FACE,{"disambiguationData":[TD([[makeQuery(id+"F45.imprint","IMPRINT",EDGE,{"derivedFrom":sQuery(id+"F45.wireOp",EDGE,"E216")}),1.0]])]});
            var Q1;
            Q1=makeQuery(id+"F45.imprint","IMPRINT",FACE,{"disambiguationData":[TD([[makeQuery(id+"F45.imprint","IMPRINT",EDGE,{"derivedFrom":sQuery(id+"F45.wireOp",EDGE,"E224")}),-1.0]])]});
            var Q2;
            Q2=sQuery(id+"F44.wireOp",EDGE,"E215");
            sweep(context, id + "F47", {"operationType" : NewBodyOperationType.REMOVE, "profiles" : qUnion([Q0, Q1]), "path" : qUnion([Q2])});
        }
    });
